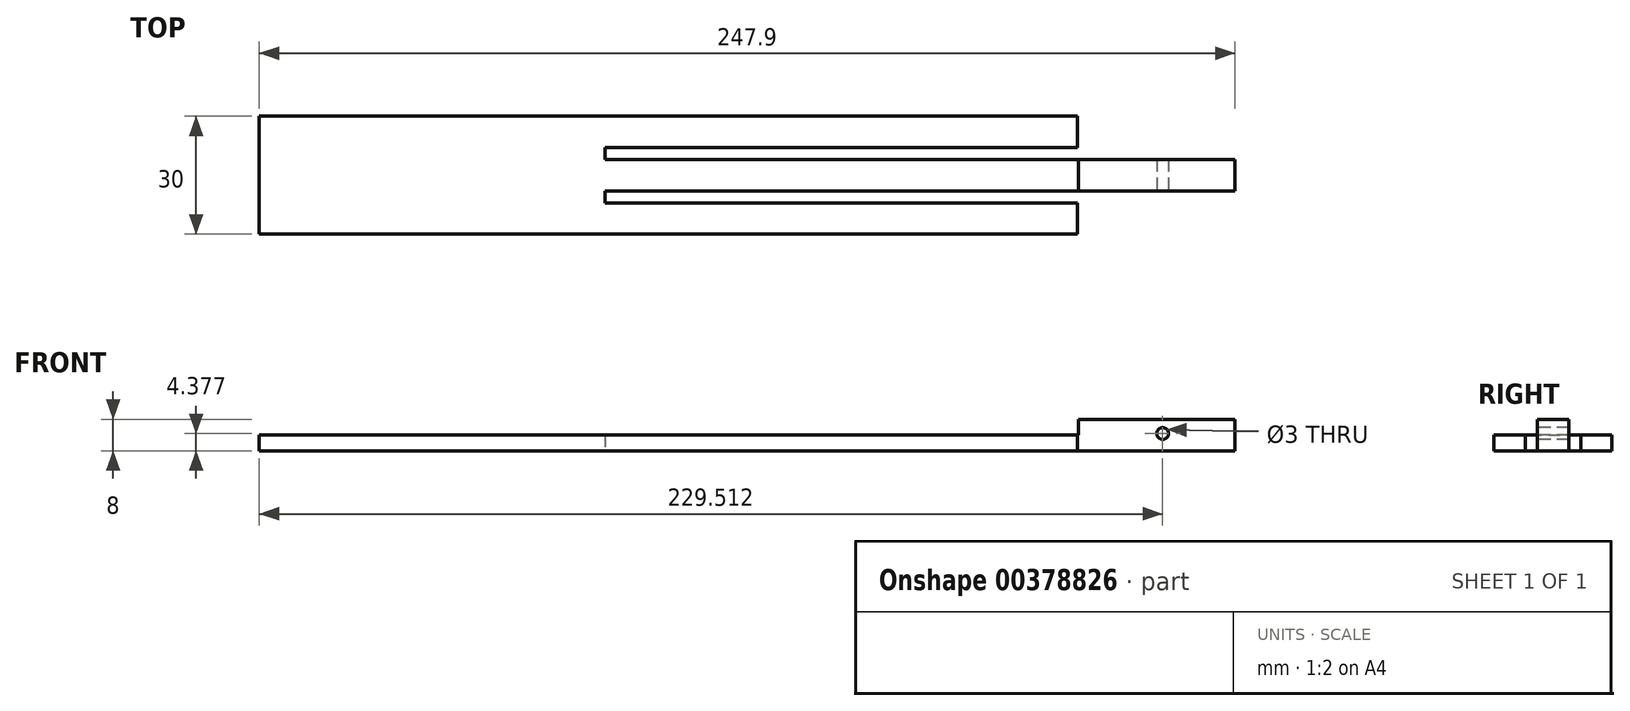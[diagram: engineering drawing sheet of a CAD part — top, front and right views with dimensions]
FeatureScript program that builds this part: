
annotation { "Feature Type Name" : "Feature", "Feature Type Description" : "" }
export const myFeature = defineFeature(function(context is Context, id is Id, definition is map)
    precondition{}
    {
        {
            var Q0;
            Q0=qCreatedBy(makeId("Top.planeOp"),FACE);
            var sketch = newSketch(context, id + "F0", { "sketchPlane" : qUnion([Q0])});
            skLineSegment(sketch, "E0.bottom", {"start": v(83.95, -15) * mm, "end": v(-123.95, -15) * mm});
            skLineSegment(sketch, "E0.top", {"start": v(83.95, 15) * mm, "end": v(-123.95, 15) * mm});
            skLineSegment(sketch, "E0.right", {"start": v(-123.95, -15) * mm, "end": v(-123.95, 15) * mm});
            skPoint(sketch, "E0.middle", {"position": v(0, 0) * mm});
            skLineSegment(sketch, "E1.bottom", {"start": v(83.95, 7) * mm, "end": v(-36.05, 7) * mm});
            skLineSegment(sketch, "E1.top", {"start": v(123.95, 4) * mm, "end": v(-36.05, 4) * mm});
            skLineSegment(sketch, "E1.right", {"start": v(-36.05, 7) * mm, "end": v(-36.05, 4) * mm});
            skLineSegment(sketch, "E2.bottom", {"start": v(123.95, -4) * mm, "end": v(-36.05, -4) * mm});
            skLineSegment(sketch, "E2.top", {"start": v(83.95, -7) * mm, "end": v(-36.05, -7) * mm});
            skLineSegment(sketch, "E2.right", {"start": v(-36.05, -4) * mm, "end": v(-36.05, -7) * mm});
            skLineSegment(sketch, "E3.trimOffspring", {"start": v(123.95, -4) * mm, "end": v(123.95, 4) * mm});
            skLineSegment(sketch, "E4.right", {"start": v(83.95, 15) * mm, "end": v(83.95, 7) * mm});
            skPoint(sketch, "E5.trimOffspring.end.orphan", {"position": v(123.95, 15) * mm});
            skLineSegment(sketch, "E6.right", {"start": v(83.95, -7) * mm, "end": v(83.95, -15) * mm});
            skPoint(sketch, "E7.orphan", {"position": v(123.95, -15) * mm});
            skSolve(sketch);
        }
        {
            var Q0;
            Q0=qSketchRegion(id+"F0",true);
            extrude(context, id + "F1", {"entities" : qUnion([Q0]), "depth" : 4 * mm});
        }
        {
            var Q0;
            Q0=makeQuery(id+"F1.opExtrude","CAP_FACE",FACE,{"disambiguationData":[OSD([sQuery(id+"F0.wireOp",EDGE,"E0.bottom"),sQuery(id+"F0.wireOp",EDGE,"E0.top"),sQuery(id+"F0.wireOp",EDGE,"E0.right"),sQuery(id+"F0.wireOp",EDGE,"E1.bottom"),sQuery(id+"F0.wireOp",EDGE,"E1.top"),sQuery(id+"F0.wireOp",EDGE,"E1.right"),sQuery(id+"F0.wireOp",EDGE,"E2.bottom"),sQuery(id+"F0.wireOp",EDGE,"E2.top"),sQuery(id+"F0.wireOp",EDGE,"E2.right"),sQuery(id+"F0.wireOp",EDGE,"E3.trimOffspring"),sQuery(id+"F0.wireOp",EDGE,"E4.right"),sQuery(id+"F0.wireOp",EDGE,"E6.right")])],"isStart":false});
            var sketch = newSketch(context, id + "F2", { "sketchPlane" : qUnion([Q0])});
            skLineSegment(sketch, "E8.bottom", {"start": v(123.95, 4) * mm, "end": v(84.13, 4) * mm});
            skLineSegment(sketch, "E8.top", {"start": v(123.95, -4) * mm, "end": v(84.13, -4) * mm});
            skLineSegment(sketch, "E8.left", {"start": v(123.95, 4) * mm, "end": v(123.95, -4) * mm});
            skLineSegment(sketch, "E8.right", {"start": v(84.13, 4) * mm, "end": v(84.13, -4) * mm});
            skSolve(sketch);
        }
        {
            var Q0;
            Q0=qSketchRegion(id+"F2",true);
            extrude(context, id + "F3", {"entities" : qUnion([Q0]), "operationType" : NewBodyOperationType.ADD, "depth" : 4 * mm});
        }
        {
            var Q0;
            Q0=makeQuery(id+"F3.boolean.opBoolean","MERGE",FACE,{"derivedFrom":[makeQuery(id+"F1.opExtrude","SWEPT_FACE",FACE,{"disambiguationData":[OSD([sQuery(id+"F0.wireOp",EDGE,"E2.bottom")])]}),makeQuery(id+"F3.opExtrude","SWEPT_FACE",FACE,{"disambiguationData":[OSD([sQuery(id+"F2.wireOp",EDGE,"E8.top")])]})]});
            var sketch = newSketch(context, id + "F4", { "sketchPlane" : qUnion([Q0])});
            skLineSegment(sketch, "E9", {"start": v(123.95, 8) * mm, "end": v(108.95, 8) * mm});
            skCircle(sketch, "E10", {"center": v(105.56, 4.38) * mm, "radius": 1.5 * mm});
            skSolve(sketch);
        }
        {
            var Q0;
            Q0=makeQuery(id+"F4.imprint","IMPRINT",FACE,{"disambiguationData":[TD([[makeQuery(id+"F4.imprint","IMPRINT",EDGE,{"derivedFrom":sQuery(id+"F4.wireOp",EDGE,"E10")}),1.0]])]});
            extrude(context, id + "F5", {"entities" : qUnion([Q0]), "operationType" : NewBodyOperationType.REMOVE, "oppositeDirection" : true, "depth" : 25 * mm});
        }
    });
